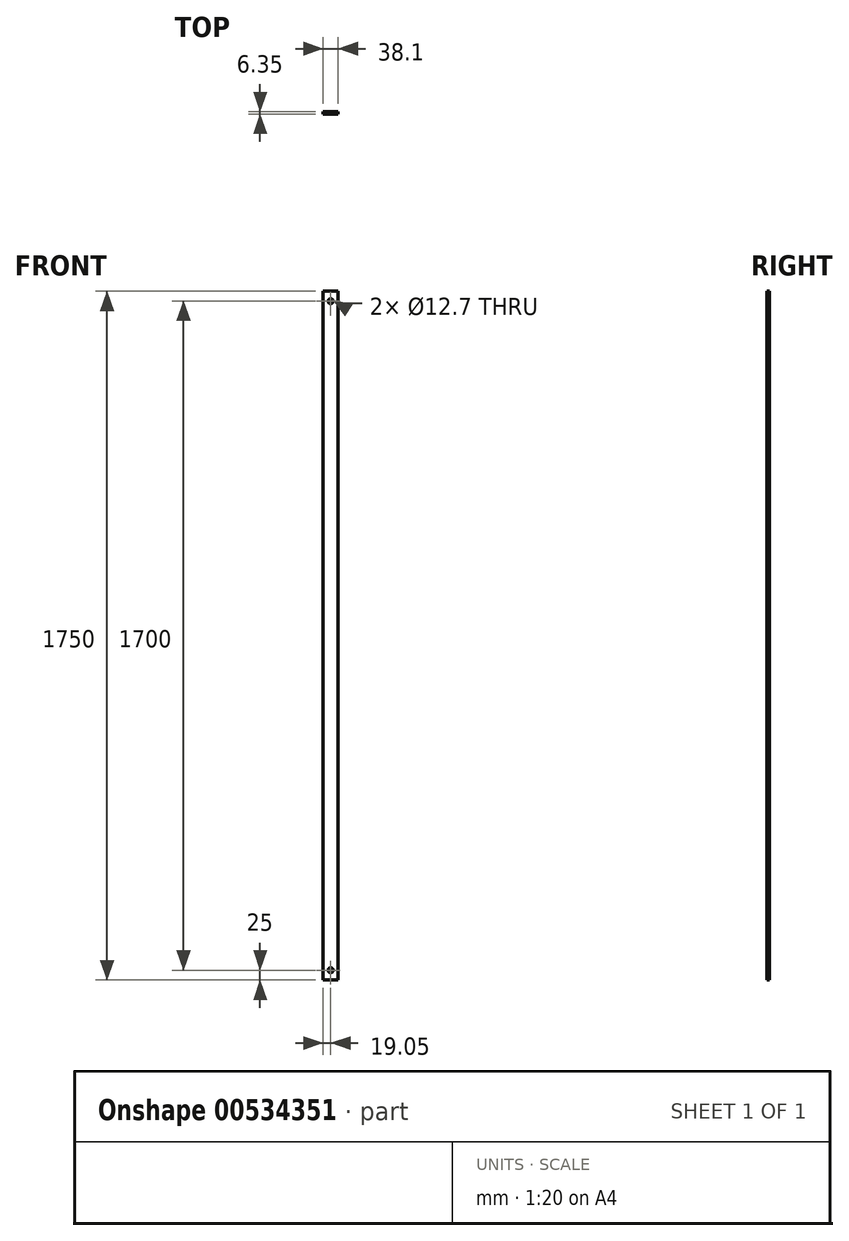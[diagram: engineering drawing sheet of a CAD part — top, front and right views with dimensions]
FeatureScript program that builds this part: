
annotation { "Feature Type Name" : "Feature", "Feature Type Description" : "" }
export const myFeature = defineFeature(function(context is Context, id is Id, definition is map)
    precondition{}
    {
        {
            var Q0;
            Q0=qCreatedBy(makeId("Front.planeOp"),FACE);
            var sketch = newSketch(context, id + "F0", { "sketchPlane" : qUnion([Q0])});
            skLineSegment(sketch, "E0", {"start": v(0, 0) * mm, "end": v(0, 1750) * mm});
            skLineSegment(sketch, "E1", {"start": v(0, 1750) * mm, "end": v(38.1, 1750) * mm});
            skLineSegment(sketch, "E2", {"start": v(38.1, 1750) * mm, "end": v(38.1, 0) * mm});
            skLineSegment(sketch, "E3", {"start": v(38.1, 0) * mm, "end": v(0, 0) * mm});
            skSolve(sketch);
        }
        {
            var Q0;
            Q0=makeQuery(id+"F0.imprint","IMPRINT",FACE,{"disambiguationData":[TD([[makeQuery(id+"F0.imprint","IMPRINT",EDGE,{"derivedFrom":sQuery(id+"F0.wireOp",EDGE,"E0")}),-1.0]])]});
            extrude(context, id + "F1", {"entities" : qUnion([Q0]), "depth" : 6.35 * mm, "offsetDistance" : 25 * mm});
        }
        {
            var Q0;
            Q0=makeQuery(id+"F1.opExtrude","CAP_FACE",FACE,{"disambiguationData":[OSD([sQuery(id+"F0.wireOp",EDGE,"E0"),sQuery(id+"F0.wireOp",EDGE,"E1"),sQuery(id+"F0.wireOp",EDGE,"E2"),sQuery(id+"F0.wireOp",EDGE,"E3")])],"isStart":false});
            var sketch = newSketch(context, id + "F2", { "sketchPlane" : qUnion([Q0])});
            skCircle(sketch, "E4", {"center": v(19.05, 1725) * mm, "radius": 6.35 * mm});
            skCircle(sketch, "E5", {"center": v(19.05, 25) * mm, "radius": 6.35 * mm});
            skLineSegment(sketch, "E6", {"start": v(19.05, 25) * mm, "end": v(19.05, 0) * mm, "construction": true});
            skLineSegment(sketch, "E7", {"start": v(19.05, 1725) * mm, "end": v(19.05, 1750) * mm, "construction": true});
            skSolve(sketch);
        }
        {
            var Q0;
            Q0=makeQuery(id+"F2.imprint","IMPRINT",FACE,{"disambiguationData":[TD([[makeQuery(id+"F2.imprint","IMPRINT",EDGE,{"derivedFrom":sQuery(id+"F2.wireOp",EDGE,"E4")}),1.0]])]});
            var Q1;
            Q1=makeQuery(id+"F2.imprint","IMPRINT",FACE,{"disambiguationData":[TD([[makeQuery(id+"F2.imprint","IMPRINT",EDGE,{"derivedFrom":sQuery(id+"F2.wireOp",EDGE,"E5")}),1.0]])]});
            extrude(context, id + "F3", {"entities" : qUnion([Q0, Q1]), "operationType" : NewBodyOperationType.REMOVE, "oppositeDirection" : true, "depth" : 25 * mm, "offsetDistance" : 25 * mm});
        }
    });
